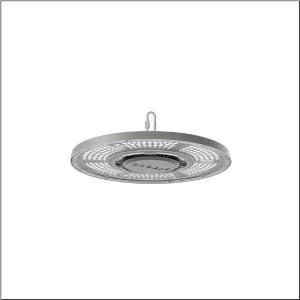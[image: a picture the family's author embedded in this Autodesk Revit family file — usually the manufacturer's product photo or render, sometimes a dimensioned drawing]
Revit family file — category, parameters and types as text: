
# Revit family: highbay_31-l_51hc42da4jmb
name_source: partatom
category: Lighting Fixtures
units: mm (PartAtom-declared; Revit-internal decimal feet)

## family parameters
Cut with Voids When Loaded = No
Host = Face
Light Source = No
Part Type = Normal
Room Calculation Point = No
Round Connector Dimension = Use Diameter
Shared = No

## types (1)
- Highbay 31-L (1 x LED, 20000 lm, 134 W, 4000K)
    Apparent Load = 134 VA
    CIE Flux Codes = 77 99 100 100 100
    Color Rendering = 80
    Color Temperature = 4000K
    Default Elevation = 1800 mm
    Description = Highbay 31-L, LED high bay luminaire, primary light control with lens, of PC, primary optical cover: cover panel, of PC, transparent, light emission: direct distribution, primary light characteristic: rotationally symmetric, installation type: suspended mounting, surface-mounted, LED, rated luminous flux: 20.000lm, luminous efficacy: 150lm/W, light colour: 840, colour temperature: 4000K, control gear: ECG DALI, with cable, 5x 1.0mm², free wire ends, mains connection: 220..240V, AC/DC, 0/50..60Hz, cable length: 1,5m, rated input power: 134W, housing, rotationally symmetric, of diecast aluminium, powder-coated, grey aluminium (RAL 9007), with hook on luminaire side, incl. screw, diameter: 404mm, protection rating (complete): IP65, insulation class (complete): insulation class I (protective earthing), certification: CE, ENEC, UKCA, protection symbol: D, impact resistance: IK08, permissible operating ambient temperature: -30..+45°C, standard: EN 60598-2-22, EN 60598, corresponds to IFS (International Featured Standards) requirements for safety and quality in the food industry, packaging unit: 1 piece
    Height = 141 mm
    Lamp = 1 x LED
    Lamp Light Flux = 20000 lm
    Lamp Power = 134 W
    Lamp count = 1
    Length = 406 mm
    Luminous efficacy = 149 lm/W
    Manufacturer = Siteco
    ModVariant = No
    Model = 51HC42DA4JMB
    Mounting Place = Ceiling
    Mounting Type = Pendant
    Number of Poles = 1
    OnlyDefault = Yes
    Power Factor = 1
    Product Name = Highbay 31-L
    Product group = LED high bay luminaire
    ProductGroupID = 903
    Protection Class = Protection class I
    Protection Degree = IP 65
    RLX_Detail_Level = 1
    RLX_Emergency_Light_Flux = 0 lm
    RLX_Emergency_Type = 0
    RLX_Emergency_Type_DB = No
    RlxData = <blob elided: 163101 chars, md5=6b48b945>
    Socket = socket
    Standby Power = 0 W
    System Light Flux = 20000 lm
    System Power = 134 W
    Type Comments = Product without accessories
    Type Image = l_1007237.jpg
    URL = http://relux.com
    VarID = ---
    Voltage = 0 V
    Weight = 0.00 kg
    Width = 0 mm  [stored 0 ft]

note: [stored X ft] marks values corroborated as IEEE doubles in the binary element streams (Revit-internal decimal feet)

## geometry (parser evidence)
native form markers: Blend x4, Sweep x10
no freeform markers — native parametric forms only
